# Revit family: РИДАН_RJIP Premium FB_FF_WG PN25 DN50-600
name_source: partatom
category: Арматура трубопроводов
units: mm (PartAtom-declared; Revit-internal decimal feet)

## family parameters
Всегда вертикально = Да
На основе рабочей плоскости = Нет
Общий = Нет
При загрузке вырезать с полостями = Нет
Размер круглого соединителя = Использовать диаметр
Тип детали = Вставляется

## types (13) — shared parameters
ADSK_Версия Revit = 2019
ADSK_Версия семейства = 1.0
ADSK_Единица измерения = шт.
ADSK_Завод-изготовитель = ООО «Ридан-Трейд»
ADSK_Количество = 1
ADSK_Потеря давления жидкости = 0.0 Па
ADSK_Расход жидкости = 0 м³/ч
LT = Table
URL = https://ridan.ru
Изготовитель = ООО «Ридан-Трейд»

## per-type parameters (varying)
- DN 50: ADSK_Диаметр условный=50 мм; ADSK_Код изделия=065N1323R; ADSK_Марка=RJIP Premium FB/FF/WG DN50; ADSK_Масса=12.38; ADSK_Наименование=RJIP Premium Кран шаровой FB FF DN50 PN25 WG; ADSK_Пропускная способность=189 м³/ч; Bot=Нет; a=28 мм; a1=3 мм; a2=17 мм; b=46 мм; c=120 мм; d=60 мм; e=101 мм; f=93 мм; g=114 мм; h=60 мм; i=90 мм; j=34 мм; k=70 мм; l=20 мм; m=165 мм; n=106 мм; o=100 мм; p=308 мм; Редуктор DN125-150=Нет; Редуктор DN200=Нет; Редуктор DN250-300=Нет; Редуктор DN350-400=Нет; Редуктор DN500=Нет; Редуктор DN50_65=Да; Редуктор DN600=Нет; Редуктор DN80-100=Нет
- DN 65: ADSK_Диаметр условный=65 мм; ADSK_Код изделия=065N1331R; ADSK_Марка=RJIP Premium FB/FF/WG DN65; ADSK_Масса=16.31; ADSK_Наименование=RJIP Premium Кран шаровой FB FF DN65 PN25 WG; ADSK_Пропускная способность=328 м³/ч; Bot=Нет; a=22 мм; a1=3 мм; a2=19 мм; b=36 мм; c=150 мм; d=75 мм; e=117 мм; f=109 мм; g=140 мм; h=76 мм; i=90 мм; j=39 мм; k=80 мм; l=20 мм; m=185 мм; n=126 мм; o=120 мм; p=310 мм; Редуктор DN125-150=Нет; Редуктор DN200=Нет; Редуктор DN250-300=Нет; Редуктор DN350-400=Нет; Редуктор DN500=Нет; Редуктор DN50_65=Нет; Редуктор DN600=Нет; Редуктор DN80-100=Да
- DN 80: ADSK_Диаметр условный=80 мм; ADSK_Код изделия=065N1336R; ADSK_Марка=RJIP Premium FB/FF/WG DN80; ADSK_Масса=20.08; ADSK_Наименование=RJIP Premium Кран шаровой FB FF DN80 PN25 WG; ADSK_Пропускная способность=494 м³/ч; Bot=Нет; a=15 мм; a1=3 мм; a2=21 мм; b=50 мм; c=160 мм; d=80 мм; e=129 мм; f=121 мм; g=159 мм; h=89 мм; i=90 мм; j=39 мм; k=96 мм; l=20 мм; m=200 мм; n=140 мм; o=134 мм; p=337 мм; Редуктор DN125-150=Нет; Редуктор DN200=Нет; Редуктор DN250-300=Нет; Редуктор DN350-400=Нет; Редуктор DN500=Нет; Редуктор DN50_65=Нет; Редуктор DN600=Нет; Редуктор DN80-100=Да
- DN 100: ADSK_Диаметр условный=100 мм; ADSK_Код изделия=065N1341R; ADSK_Марка=RJIP Premium FB/FF/WG DN100; ADSK_Масса=29.18; ADSK_Наименование=RJIP Premium Кран шаровой FB FF DN100 PN25 WG; ADSK_Пропускная способность=1358 м³/ч; Bot=Нет; a=5 мм; a1=3 мм; a2=23 мм; b=44 мм; c=183 мм; d=92 мм; e=142 мм; f=129 мм; g=180 мм; h=108 мм; i=125 мм; j=49 мм; k=113 мм; l=20 мм; m=235 мм; n=166 мм; o=160 мм; p=332 мм; Редуктор DN125-150=Да; Редуктор DN200=Нет; Редуктор DN250-300=Нет; Редуктор DN350-400=Нет; Редуктор DN500=Нет; Редуктор DN50_65=Нет; Редуктор DN600=Нет; Редуктор DN80-100=Нет
- DN 125: ADSK_Диаметр условный=125 мм; ADSK_Код изделия=065N1346R; ADSK_Марка=RJIP Premium FB/FF/WG DN125; ADSK_Масса=40.65; ADSK_Наименование=RJIP Premium Кран шаровой FB FF DN125 PN25 WG; ADSK_Пропускная способность=2156 м³/ч; Bot=Нет; a=16 мм; a1=3 мм; a2=25 мм; b=29 мм; c=220 мм; d=110 мм; e=162 мм; f=149 мм; g=219 мм; h=133 мм; i=125 мм; j=49 мм; k=129 мм; l=20 мм; m=270 мм; n=192 мм; o=186 мм; p=366 мм; Редуктор DN125-150=Да; Редуктор DN200=Нет; Редуктор DN250-300=Нет; Редуктор DN350-400=Нет; Редуктор DN500=Нет; Редуктор DN50_65=Нет; Редуктор DN600=Нет; Редуктор DN80-100=Нет
- DN 150: ADSK_Диаметр условный=150 мм; ADSK_Код изделия=065N1351R; ADSK_Марка=RJIP Premium FB/FF/WG DN150; ADSK_Масса=94.4; ADSK_Наименование=RJIP Premium Кран шаровой FB FF DN150 PN25 WG; ADSK_Пропускная способность=2372 м³/ч; Bot=Да; a=6 мм; a1=3 мм; a2=27 мм; b=82 мм; c=270 мм; d=135 мм; e=215 мм; f=197 мм; g=273 мм; h=159 мм; i=150 мм; j=78 мм; k=185 мм; l=48 мм; m=300 мм; n=220 мм; o=214 мм; p=506 мм; Редуктор DN125-150=Нет; Редуктор DN200=Да; Редуктор DN250-300=Нет; Редуктор DN350-400=Нет; Редуктор DN500=Нет; Редуктор DN50_65=Нет; Редуктор DN600=Нет; Редуктор DN80-100=Нет
- DN 200: ADSK_Диаметр условный=200 мм; ADSK_Код изделия=065N1356R; ADSK_Марка=RJIP Premium FB/FF/WG DN200; ADSK_Масса=127; ADSK_Наименование=RJIP Premium Кран шаровой FB FF DN200 PN25 WG; ADSK_Пропускная способность=3698 м³/ч; Bot=Да; a=25 мм; a1=3 мм; a2=29 мм; b=56 мм; c=390 мм; d=195 мм; e=254 мм; f=236 мм; g=351 мм; h=219 мм; i=210 мм; j=78 мм; k=224 мм; l=48 мм; m=360 мм; n=280 мм; o=274 мм; p=615 мм; Редуктор DN125-150=Нет; Редуктор DN200=Нет; Редуктор DN250-300=Да; Редуктор DN350-400=Нет; Редуктор DN500=Нет; Редуктор DN50_65=Нет; Редуктор DN600=Нет; Редуктор DN80-100=Нет
- DN 250: ADSK_Диаметр условный=250 мм; ADSK_Код изделия=065N1361R; ADSK_Марка=RJIP Premium FB/FF/WG DN250; ADSK_Масса=251.3; ADSK_Наименование=RJIP Premium Кран шаровой FB FF DN250 PN25 WG; ADSK_Пропускная способность=5725 м³/ч; Bot=Да; a=25 мм; a1=3 мм; a2=32 мм; b=43 мм; c=500 мм; d=250 мм; e=302 мм; f=284 мм; g=426 мм; h=273 мм; i=210 мм; j=88 мм; k=278 мм; l=62 мм; m=425 мм; n=338 мм; o=332 мм; p=705 мм; Редуктор DN125-150=Нет; Редуктор DN200=Нет; Редуктор DN250-300=Да; Редуктор DN350-400=Нет; Редуктор DN500=Нет; Редуктор DN50_65=Нет; Редуктор DN600=Нет; Редуктор DN80-100=Нет
- DN 300: ADSK_Диаметр условный=300 мм; ADSK_Код изделия=065N1366R; ADSK_Марка=RJIP Premium FB/FF/WG DN300; ADSK_Масса=362.3; ADSK_Наименование=RJIP Premium Кран шаровой FB FF DN300 PN25 WG; ADSK_Пропускная способность=22560 м³/ч; Bot=Да; a=97 мм; a1=4 мм; a2=34 мм; b=63 мм; c=387 мм; d=193 мм; e=347 мм; f=329 мм; g=505 мм; h=325 мм; i=210 мм; j=98 мм; k=340 мм; l=100 мм; m=485 мм; n=398 мм; o=390 мм; p=782 мм; Редуктор DN125-150=Нет; Редуктор DN200=Нет; Редуктор DN250-300=Нет; Редуктор DN350-400=Да; Редуктор DN500=Нет; Редуктор DN50_65=Нет; Редуктор DN600=Нет; Редуктор DN80-100=Нет
- DN 350: ADSK_Диаметр условный=350 мм; ADSK_Код изделия=065N1373R; ADSK_Марка=RJIP Premium FB/FF/WG DN350; ADSK_Масса=469.6; ADSK_Наименование=RJIP Premium Кран шаровой FB FF DN350 PN25 WG; ADSK_Пропускная способность=27680 м³/ч; Bot=Да; a=101 мм; a1=4 мм; a2=38 мм; b=76 мм; c=425 мм; d=212 мм; e=383 мм; f=365 мм; g=556 мм; h=377 мм; i=210 мм; j=124 мм; k=365 мм; l=100 мм; m=555 мм; n=454 мм; o=446 мм; p=862 мм; Редуктор DN125-150=Нет; Редуктор DN200=Нет; Редуктор DN250-300=Нет; Редуктор DN350-400=Да; Редуктор DN500=Нет; Редуктор DN50_65=Нет; Редуктор DN600=Нет; Редуктор DN80-100=Нет
- DN 400: ADSK_Диаметр условный=400 мм; ADSK_Код изделия=065N1376R; ADSK_Марка=RJIP Premium FB/FF/WG DN400; ADSK_Масса=492.8; ADSK_Наименование=RJIP Premium Кран шаровой FB FF DN400 PN25 WG; ADSK_Пропускная способность=35050 м³/ч; Bot=Да; a=81 мм; a1=4 мм; a2=44 мм; b=91 мм; c=497 мм; d=249 мм; e=446 мм; f=421 мм; g=676 мм; h=426 мм; i=300 мм; j=150 мм; k=462 мм; l=125 мм; m=620 мм; n=512 мм; o=504 мм; p=939 мм; Редуктор DN125-150=Нет; Редуктор DN200=Нет; Редуктор DN250-300=Нет; Редуктор DN350-400=Нет; Редуктор DN500=Да; Редуктор DN50_65=Нет; Редуктор DN600=Нет; Редуктор DN80-100=Нет
- DN 500: ADSK_Диаметр условный=500 мм; ADSK_Код изделия=065N1383R; ADSK_Марка=RJIP Premium FB/FF/WG DN500; ADSK_Масса=1248.3; ADSK_Наименование=RJIP Premium Кран шаровой FB FF DN500 PN25 WG; ADSK_Пропускная способность=55005 м³/ч; Bot=Да; a=122 мм; a1=4 мм; a2=54 мм; b=109 мм; c=589 мм; d=295 мм; e=529 мм; f=501 мм; g=808 мм; h=530 мм; i=350 мм; j=165 мм; k=490 мм; l=125 мм; m=730 мм; n=622 мм; o=614 мм; p=1167 мм; Редуктор DN125-150=Нет; Редуктор DN200=Нет; Редуктор DN250-300=Нет; Редуктор DN350-400=Нет; Редуктор DN500=Нет; Редуктор DN50_65=Нет; Редуктор DN600=Да; Редуктор DN80-100=Нет
- DN 600: ADSK_Диаметр условный=600 мм; ADSK_Код изделия=065N1386R; ADSK_Марка=RJIP Premium FB/FF/WG DN600; ADSK_Масса=2107; ADSK_Наименование=RJIP Premium Кран шаровой FB FF DN600 PN25 WG; ADSK_Пропускная способность=91500 м³/ч; Bot=Да; a=207 мм; a1=5 мм; a2=63 мм; b=90 мм; c=675 мм; d=337 мм; e=623 мм; f=595 мм; g=1012 мм; h=630 мм; i=350 мм; j=177 мм; k=629 мм; l=138 мм; m=845 мм; n=730 мм; o=720 мм; p=1404 мм; Редуктор DN125-150=Нет; Редуктор DN200=Нет; Редуктор DN250-300=Нет; Редуктор DN350-400=Нет; Редуктор DN500=Нет; Редуктор DN50_65=Нет; Редуктор DN600=Да; Редуктор DN80-100=Нет
